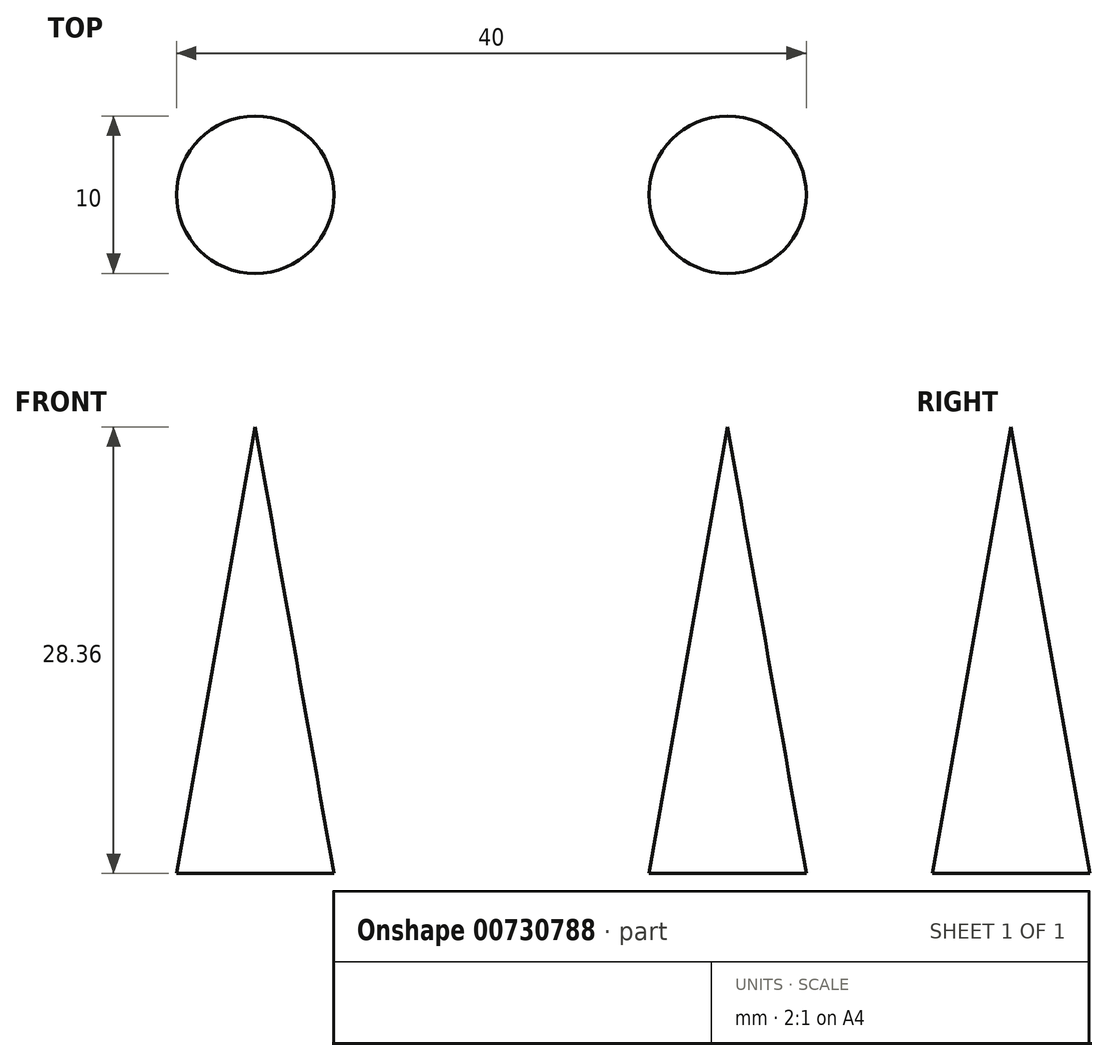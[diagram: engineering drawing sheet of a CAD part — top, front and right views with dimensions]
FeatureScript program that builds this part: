
annotation { "Feature Type Name" : "Feature", "Feature Type Description" : "" }
export const myFeature = defineFeature(function(context is Context, id is Id, definition is map)
    precondition{}
    {
        {
            var Q0;
            Q0=qCreatedBy(makeId("Top.planeOp"),FACE);
            var sketch = newSketch(context, id + "F0", { "sketchPlane" : qUnion([Q0])});
            skCircle(sketch, "E0", {"center": v(-15, 0) * mm, "radius": 5 * mm});
            skCircle(sketch, "E1", {"center": v(15, 0) * mm, "radius": 5 * mm});
            skSolve(sketch);
        }
        {
            var Q0;
            Q0=makeQuery(id+"F0.imprint","IMPRINT",FACE,{"disambiguationData":[TD([[makeQuery(id+"F0.imprint","IMPRINT",EDGE,{"derivedFrom":sQuery(id+"F0.wireOp",EDGE,"E0")}),1.0]])]});
            var Q1;
            Q1=makeQuery(id+"F0.imprint","IMPRINT",FACE,{"disambiguationData":[TD([[makeQuery(id+"F0.imprint","IMPRINT",EDGE,{"derivedFrom":sQuery(id+"F0.wireOp",EDGE,"E1")}),1.0]])]});
            extrude(context, id + "F1", {"entities" : qUnion([Q0, Q1]), "depth" : 30 * mm, "offsetDistance" : 25 * mm, "hasDraft" : true, "draftAngle" : 10 * degree, "draftPullDirection" : true});
        }
    });
